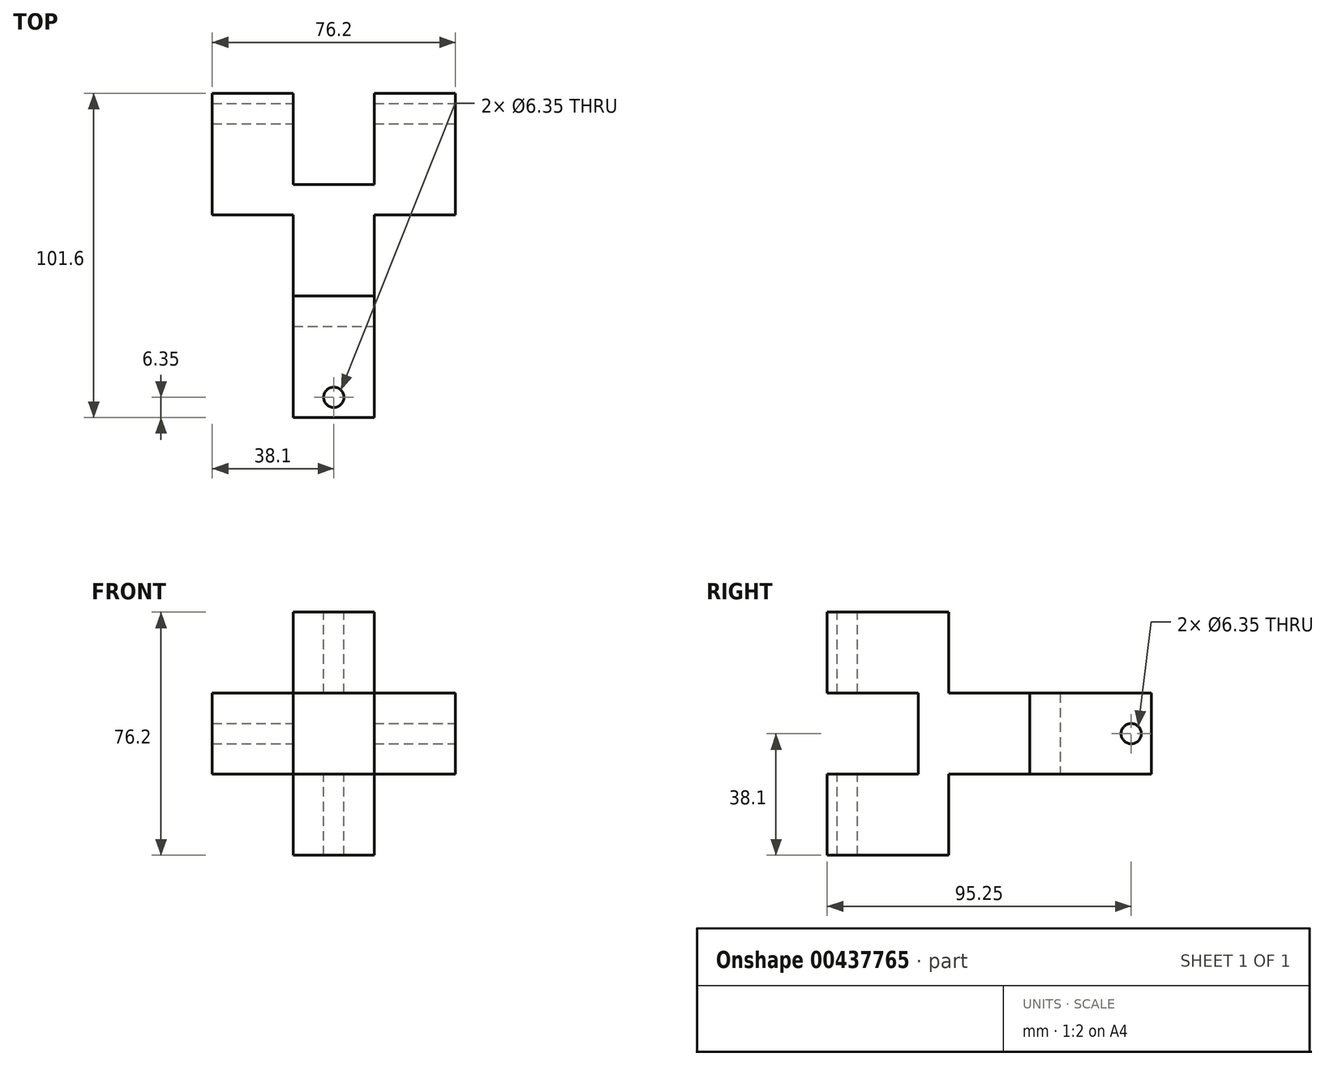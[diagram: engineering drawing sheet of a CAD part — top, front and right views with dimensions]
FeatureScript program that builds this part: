
annotation { "Feature Type Name" : "Feature", "Feature Type Description" : "" }
export const myFeature = defineFeature(function(context is Context, id is Id, definition is map)
    precondition{}
    {
        {
            var Q0;
            Q0=qCreatedBy(makeId("Front.planeOp"),FACE);
            var sketch = newSketch(context, id + "F0", { "sketchPlane" : qUnion([Q0])});
            skLineSegment(sketch, "E0.bottom", {"start": v(-25.4, 25.4) * mm, "end": v(0, 25.4) * mm});
            skLineSegment(sketch, "E0.top", {"start": v(-25.4, 0) * mm, "end": v(0, 0) * mm});
            skLineSegment(sketch, "E0.left", {"start": v(-25.4, 25.4) * mm, "end": v(-25.4, 0) * mm});
            skLineSegment(sketch, "E0.right", {"start": v(0, 25.4) * mm, "end": v(0, 0) * mm});
            skSolve(sketch);
        }
        {
            var Q0;
            Q0=makeQuery(id+"F0.imprint","IMPRINT",FACE,{"disambiguationData":[TD([[makeQuery(id+"F0.imprint","IMPRINT",EDGE,{"derivedFrom":sQuery(id+"F0.wireOp",EDGE,"E0.bottom")}),-1.0]])]});
            extrude(context, id + "F1", {"entities" : qUnion([Q0]), "depth" : 25.4 * mm});
        }
        {
            var Q0;
            Q0=qCreatedBy(makeId("Top.planeOp"),FACE);
            var sketch = newSketch(context, id + "F2", { "sketchPlane" : qUnion([Q0])});
            skLineSegment(sketch, "E1.bottom", {"start": v(25.4, 38.1) * mm, "end": v(0, 38.1) * mm});
            skLineSegment(sketch, "E1.top", {"start": v(25.4, 0) * mm, "end": v(-50.8, 0) * mm});
            skLineSegment(sketch, "E1.left", {"start": v(25.4, 38.1) * mm, "end": v(25.4, 0) * mm});
            skLineSegment(sketch, "E1.right", {"start": v(-50.8, 38.1) * mm, "end": v(-50.8, 0) * mm});
            skLineSegment(sketch, "E2.top", {"start": v(0, 9.53) * mm, "end": v(-25.4, 9.53) * mm});
            skLineSegment(sketch, "E2.left", {"start": v(0, 38.1) * mm, "end": v(0, 9.53) * mm});
            skLineSegment(sketch, "E2.right", {"start": v(-25.4, 38.1) * mm, "end": v(-25.4, 9.53) * mm});
            skLineSegment(sketch, "E3.trimOffspring", {"start": v(-25.4, 38.1) * mm, "end": v(-50.8, 38.1) * mm});
            skSolve(sketch);
        }
        {
            var Q0;
            Q0 = qSketchRegion(id + "F2", true);
            extrude(context, id + "F3", {"entities" : qUnion([Q0]), "operationType" : NewBodyOperationType.ADD, "depth" : 25.4 * mm});
        }
        {
            var Q0;
            Q0=makeQuery(id+"F1.opExtrude","CAP_FACE",FACE,{"disambiguationData":[OSD([sQuery(id+"F0.wireOp",EDGE,"E0.bottom"),sQuery(id+"F0.wireOp",EDGE,"E0.top"),sQuery(id+"F0.wireOp",EDGE,"E0.left"),sQuery(id+"F0.wireOp",EDGE,"E0.right")])],"isStart":false});
            var sketch = newSketch(context, id + "F4", { "sketchPlane" : qUnion([Q0])});
            skLineSegment(sketch, "E4.bottom", {"start": v(25.4, 50.8) * mm, "end": v(-50.8, 50.8) * mm});
            skLineSegment(sketch, "E4.top", {"start": v(25.4, -25.4) * mm, "end": v(-50.8, -25.4) * mm});
            skLineSegment(sketch, "E4.left", {"start": v(25.4, 50.8) * mm, "end": v(25.4, -25.4) * mm});
            skLineSegment(sketch, "E4.right", {"start": v(-50.8, 50.8) * mm, "end": v(-50.8, -25.4) * mm});
            skSolve(sketch);
        }
        {
            var Q0;
            Q0 = qSketchRegion(id + "F4", true);
            extrude(context, id + "F5", {"entities" : qUnion([Q0]), "operationType" : NewBodyOperationType.ADD, "depth" : 38.1 * mm});
        }
        {
            var Q0;
            Q0=makeQuery(id+"F5.opExtrude","SWEPT_FACE",FACE,{"disambiguationData":[OSD([sQuery(id+"F4.wireOp",EDGE,"E4.bottom")])]});
            var sketch = newSketch(context, id + "F6", { "sketchPlane" : qUnion([Q0])});
            skLineSegment(sketch, "E5.bottom", {"start": v(25.4, -25.4) * mm, "end": v(-50.8, -25.4) * mm});
            skLineSegment(sketch, "E5.top", {"start": v(25.4, -63.5) * mm, "end": v(0, -63.5) * mm});
            skLineSegment(sketch, "E5.left", {"start": v(25.4, -25.4) * mm, "end": v(25.4, -63.5) * mm});
            skLineSegment(sketch, "E5.right", {"start": v(-50.8, -25.4) * mm, "end": v(-50.8, -63.5) * mm});
            skLineSegment(sketch, "E6", {"start": v(-25.4, -25.4) * mm, "end": v(-25.4, -63.5) * mm});
            skLineSegment(sketch, "E7", {"start": v(0, -25.4) * mm, "end": v(0, -63.5) * mm});
            skLineSegment(sketch, "E8.trimOffspring", {"start": v(-25.4, -63.5) * mm, "end": v(-50.8, -63.5) * mm});
            skSolve(sketch);
        }
        {
            var Q0;
            Q0 = qSketchRegion(id + "F6", true);
            extrude(context, id + "F7", {"entities" : qUnion([Q0]), "operationType" : NewBodyOperationType.REMOVE, "oppositeDirection" : true, "depth" : 101.6 * mm});
        }
        {
            var Q0;
            Q0=makeQuery(id+"F7.boolean.opBoolean","MERGE",FACE,{"derivedFrom":[makeQuery(id+"F1.opExtrude","SWEPT_FACE",FACE,{"disambiguationData":[OSD([sQuery(id+"F0.wireOp",EDGE,"E0.right")])]}),makeQuery(id+"F7.opExtrude","SWEPT_FACE",FACE,{"disambiguationData":[OSD([sQuery(id+"F6.wireOp",EDGE,"E7")])]})]});
            var sketch = newSketch(context, id + "F8", { "sketchPlane" : qUnion([Q0])});
            skLineSegment(sketch, "E9.bottom", {"start": v(-63.5, 25.4) * mm, "end": v(-34.92, 25.4) * mm});
            skLineSegment(sketch, "E9.top", {"start": v(-63.5, 0) * mm, "end": v(-34.92, 0) * mm});
            skLineSegment(sketch, "E9.left", {"start": v(-63.5, 25.4) * mm, "end": v(-63.5, 0) * mm});
            skLineSegment(sketch, "E9.right", {"start": v(-34.93, 25.4) * mm, "end": v(-34.93, 0) * mm});
            skSolve(sketch);
        }
        {
            var Q0;
            Q0 = qSketchRegion(id + "F8", true);
            extrude(context, id + "F9", {"entities" : qUnion([Q0]), "operationType" : NewBodyOperationType.REMOVE, "oppositeDirection" : true, "depth" : 25.4 * mm});
        }
        {
            var Q0;
            Q0=makeQuery(id+"F5.opExtrude","SWEPT_FACE",FACE,{"disambiguationData":[OSD([sQuery(id+"F4.wireOp",EDGE,"E4.bottom")])]});
            var sketch = newSketch(context, id + "F10", { "sketchPlane" : qUnion([Q0])});
            skCircle(sketch, "E10", {"center": v(-12.7, -57.15) * mm, "radius": 3.18 * mm});
            skSolve(sketch);
        }
        {
            var Q0;
            Q0 = qSketchRegion(id + "F10", true);
            extrude(context, id + "F11", {"entities" : qUnion([Q0]), "operationType" : NewBodyOperationType.REMOVE, "oppositeDirection" : true, "depth" : 101.6 * mm});
        }
        {
            var Q0;
            Q0=makeQuery(id+"F3.opExtrude","SWEPT_FACE",FACE,{"disambiguationData":[OSD([sQuery(id+"F2.wireOp",EDGE,"E1.left")])]});
            var sketch = newSketch(context, id + "F12", { "sketchPlane" : qUnion([Q0])});
            skCircle(sketch, "E11", {"center": v(31.75, 12.7) * mm, "radius": 3.17 * mm});
            skSolve(sketch);
        }
        {
            var Q0;
            Q0 = qSketchRegion(id + "F12", true);
            extrude(context, id + "F13", {"entities" : qUnion([Q0]), "operationType" : NewBodyOperationType.REMOVE, "oppositeDirection" : true, "depth" : 127 * mm});
        }
    });
